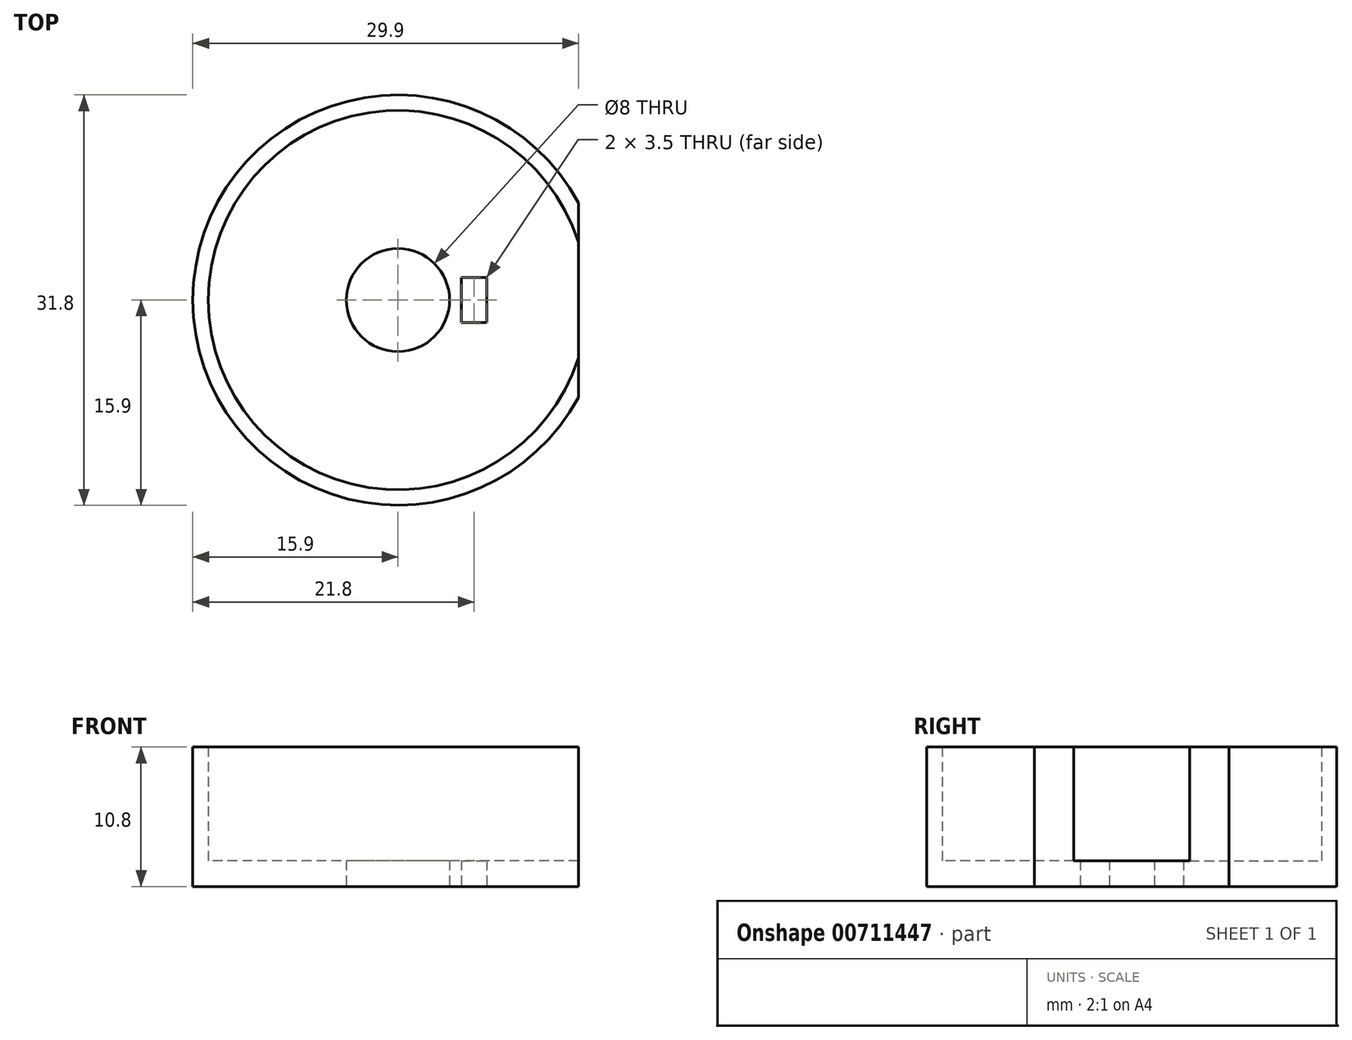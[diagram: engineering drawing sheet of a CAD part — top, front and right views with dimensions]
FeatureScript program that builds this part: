
annotation { "Feature Type Name" : "Feature", "Feature Type Description" : "" }
export const myFeature = defineFeature(function(context is Context, id is Id, definition is map)
    precondition{}
    {
        {
            var Q0;
            Q0=qCreatedBy(makeId("Top.planeOp"),FACE);
            var sketch = newSketch(context, id + "F0", { "sketchPlane" : qUnion([Q0])});
            skCircle(sketch, "E0", {"center": v(0, 0) * mm, "radius": 15.9 * mm});
            skCircle(sketch, "E1", {"center": v(0, 0) * mm, "radius": 4 * mm});
            skSolve(sketch);
        }
        {
            var Q0;
            Q0=makeQuery(id+"F0.imprint","IMPRINT",FACE,{"disambiguationData":[TD([[makeQuery(id+"F0.imprint","IMPRINT",EDGE,{"derivedFrom":sQuery(id+"F0.wireOp",EDGE,"E0")}),1.0]])]});
            var Q1;
            Q1=makeQuery(id+"F0.imprint","IMPRINT",FACE,{"disambiguationData":[TD([[makeQuery(id+"F0.imprint","IMPRINT",EDGE,{"derivedFrom":sQuery(id+"F0.wireOp",EDGE,"E1")}),1.0]])]});
            var Q2;
            {var subQ0=sQuery(id+"F0.wireOp",EDGE,"Zi9mBCza-bUwp-INGQ-UDxA-Ya5TlcSwkcdq");Q2=makeQuery(id+"F0.imprint","IMPRINT",FACE,{"disambiguationData":[TD([[makeQuery(id+"F0.imprint","IMPRINT",EDGE,{"derivedFrom":subQ0}),1.0]])]});}
            var Q3;
            {var subQ0=sQuery(id+"F0.wireOp",EDGE,"Zi9mBCza-bUwp-INGQ-UDxA-Ya5TlcSwkcdq");Q3=makeQuery(id+"F0.imprint","IMPRINT",FACE,{"disambiguationData":[TD([[makeQuery(id+"F0.imprint","IMPRINT",EDGE,{"derivedFrom":subQ0}),-1.0]])]});}
            extrude(context, id + "F1", {"entities" : qUnion([Q0, Q1, Q2, Q3]), "depth" : 10 * mm, "offsetDistance" : 25 * mm});
        }
        {
            var Q0;
            Q0=makeQuery(id+"F1.opExtrude","CAP_FACE",FACE,{"disambiguationData":[OSD([sQuery(id+"F0.wireOp",EDGE,"E0")])],"isStart":false});
            shell(context, id + "F2", {"entities" : qUnion([Q0]), "thickness" : 1.2 * mm});
        }
        {
            var Q0;
            Q0=makeQuery(id+"F0.imprint","IMPRINT",FACE,{"disambiguationData":[TD([[makeQuery(id+"F0.imprint","IMPRINT",EDGE,{"derivedFrom":sQuery(id+"F0.wireOp",EDGE,"E1")}),1.0]])]});
            var Q1;
            Q1=sQuery(id+"F0.wireOp",EDGE,"E1");
            extrude(context, id + "F3", {"entities" : qUnion([Q0]), "operationType" : NewBodyOperationType.REMOVE, "surfaceEntities" : qUnion([Q1]), "endBound" : BoundingType.THROUGH_ALL, "depth" : 25 * mm, "offsetDistance" : 25 * mm});
        }
        {
            var Q0;
            Q0=makeQuery(id+"F0.imprint","IMPRINT",FACE,{"disambiguationData":[TD([[makeQuery(id+"F0.imprint","IMPRINT",EDGE,{"derivedFrom":sQuery(id+"F0.wireOp",EDGE,"E0")}),1.0]])]});
            extrude(context, id + "F4", {"entities" : qUnion([Q0]), "operationType" : NewBodyOperationType.ADD, "oppositeDirection" : true, "depth" : 0.8 * mm, "offsetDistance" : 25 * mm});
        }
        {
            var Q0;
            Q0=makeQuery(id+"F4.opExtrude","CAP_FACE",FACE,{"disambiguationData":[OSD([sQuery(id+"F0.wireOp",EDGE,"E0"),sQuery(id+"F0.wireOp",EDGE,"E1")])],"isStart":false});
            var sketch = newSketch(context, id + "F5", { "sketchPlane" : qUnion([Q0])});
            skLineSegment(sketch, "E2", {"start": v(14, 7.54) * mm, "end": v(14, -7.54) * mm});
            skCircle(sketch, "E3", {"center": v(0, 0) * mm, "radius": 15.9 * mm});
            skCircle(sketch, "E4", {"center": v(0, 0) * mm, "radius": 4 * mm});
            skLineSegment(sketch, "E5.bottom", {"start": v(6.9, -1.75) * mm, "end": v(4.9, -1.75) * mm});
            skLineSegment(sketch, "E5.top", {"start": v(6.9, 1.75) * mm, "end": v(4.9, 1.75) * mm});
            skLineSegment(sketch, "E5.left", {"start": v(6.9, -1.75) * mm, "end": v(6.9, 1.75) * mm});
            skLineSegment(sketch, "E5.right", {"start": v(4.9, -1.75) * mm, "end": v(4.9, 1.75) * mm});
            skPoint(sketch, "E5.middle", {"position": v(5.9, 0) * mm});
            skSolve(sketch);
        }
        {
            var Q0;
            Q0=makeQuery(id+"F5.imprint","IMPRINT",FACE,{"disambiguationData":[TD([[makeQuery(id+"F5.imprint","IMPRINT",EDGE,{"derivedFrom":sQuery(id+"F5.wireOp",EDGE,"E5.bottom")}),-1.0]])]});
            var Q1;
            {var subQ0=sQuery(id+"F5.wireOp",EDGE,"E2");Q1=makeQuery(id+"F5.imprint","IMPRINT",FACE,{"disambiguationData":[TD([[makeQuery(id+"F5.imprint","IMPRINT",EDGE,{"derivedFrom":subQ0}),1.0]])]});}
            extrude(context, id + "F6", {"entities" : qUnion([Q0, Q1]), "operationType" : NewBodyOperationType.REMOVE, "endBound" : BoundingType.THROUGH_ALL, "oppositeDirection" : true, "depth" : 25 * mm, "offsetDistance" : 25 * mm});
        }
    });
